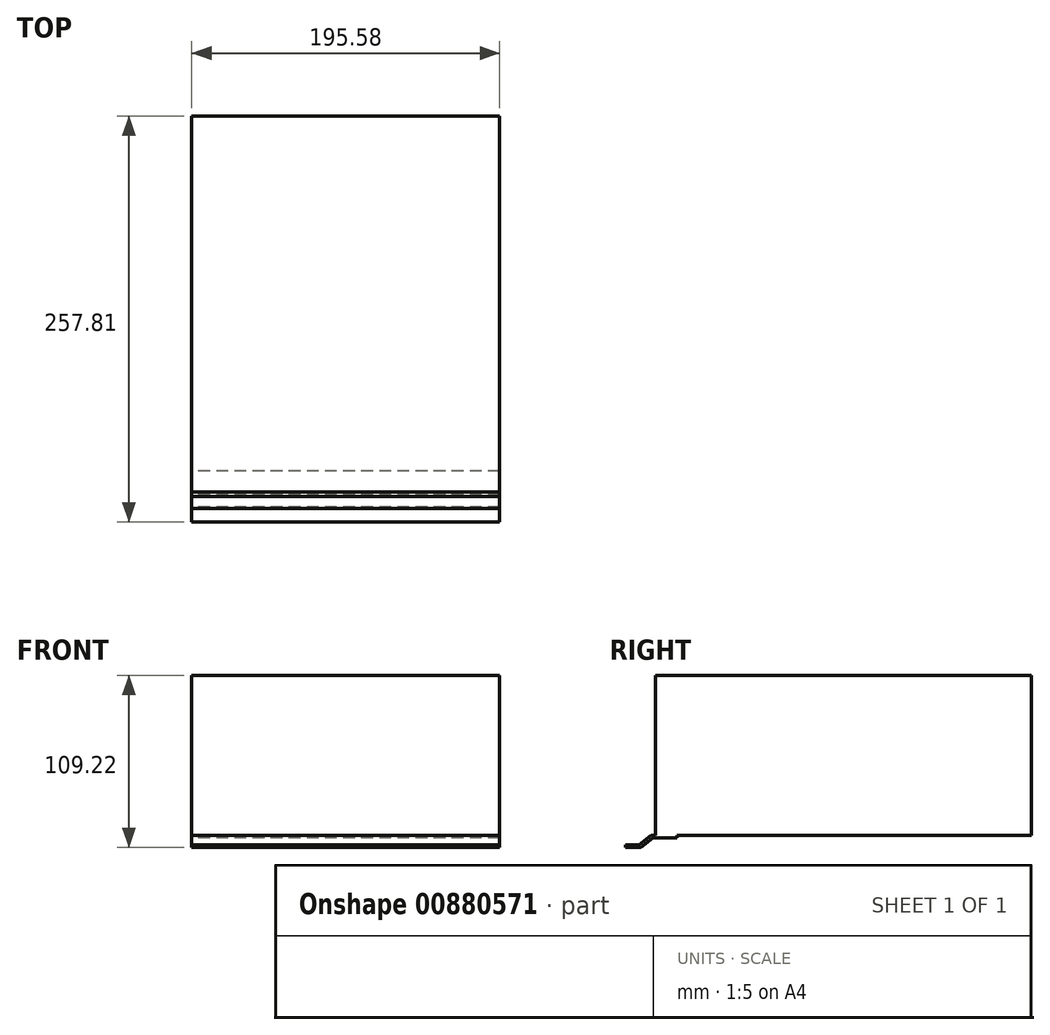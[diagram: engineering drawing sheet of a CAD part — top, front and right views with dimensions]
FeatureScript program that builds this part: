
annotation { "Feature Type Name" : "Feature", "Feature Type Description" : "" }
export const myFeature = defineFeature(function(context is Context, id is Id, definition is map)
    precondition{}
    {
        {
            var Q0;
            Q0=qCreatedBy(makeId("Top.planeOp"),FACE);
            var sketch = newSketch(context, id + "F0", { "sketchPlane" : qUnion([Q0])});
            skLineSegment(sketch, "E0.bottom", {"start": v(97.8, 119.38) * mm, "end": v(-97.8, 119.38) * mm});
            skLineSegment(sketch, "E0.top", {"start": v(97.8, -119.38) * mm, "end": v(-97.8, -119.38) * mm});
            skLineSegment(sketch, "E0.left", {"start": v(97.8, 119.38) * mm, "end": v(97.8, -119.38) * mm});
            skLineSegment(sketch, "E0.right", {"start": v(-97.8, 119.38) * mm, "end": v(-97.8, -119.38) * mm});
            skPoint(sketch, "E0.middle", {"position": v(0, 0) * mm});
            skSolve(sketch);
        }
        {
            var Q0;
            Q0=qSketchRegion(id+"F0",true);
            extrude(context, id + "F1", {"entities" : qUnion([Q0]), "depth" : 101.6 * mm, "offsetDistance" : 25.4 * mm});
        }
        {
            var Q0;
            Q0=makeQuery(id+"F1.opExtrude","SWEPT_FACE",FACE,{"disambiguationData":[OSD([sQuery(id+"F0.wireOp",EDGE,"E0.right")])]});
            var sketch = newSketch(context, id + "F2", { "sketchPlane" : qUnion([Q0])});
            skLineSegment(sketch, "E1", {"start": v(105.9, 0) * mm, "end": v(122.35, 0) * mm});
            skLineSegment(sketch, "E2", {"start": v(122.35, 0) * mm, "end": v(129.94, -6.03) * mm});
            skLineSegment(sketch, "E3", {"start": v(129.94, -6.03) * mm, "end": v(138.43, -6.03) * mm});
            skLineSegment(sketch, "E4", {"start": v(138.43, -6.03) * mm, "end": v(138.43, -7.62) * mm});
            skLineSegment(sketch, "E5", {"start": v(138.43, -7.62) * mm, "end": v(128.8, -7.62) * mm});
            skLineSegment(sketch, "E6", {"start": v(128.8, -7.62) * mm, "end": v(121.2, -1.59) * mm});
            skLineSegment(sketch, "E7", {"start": v(121.2, -1.59) * mm, "end": v(105.9, -1.59) * mm});
            skLineSegment(sketch, "E8", {"start": v(105.9, -1.59) * mm, "end": v(105.9, 0) * mm});
            skSolve(sketch);
        }
        {
            var Q0;
            Q0=qSketchRegion(id+"F2",true);
            extrude(context, id + "F3", {"entities" : qUnion([Q0]), "operationType" : NewBodyOperationType.ADD, "oppositeDirection" : true, "depth" : 195.58 * mm, "offsetDistance" : 25.4 * mm});
        }
    });
